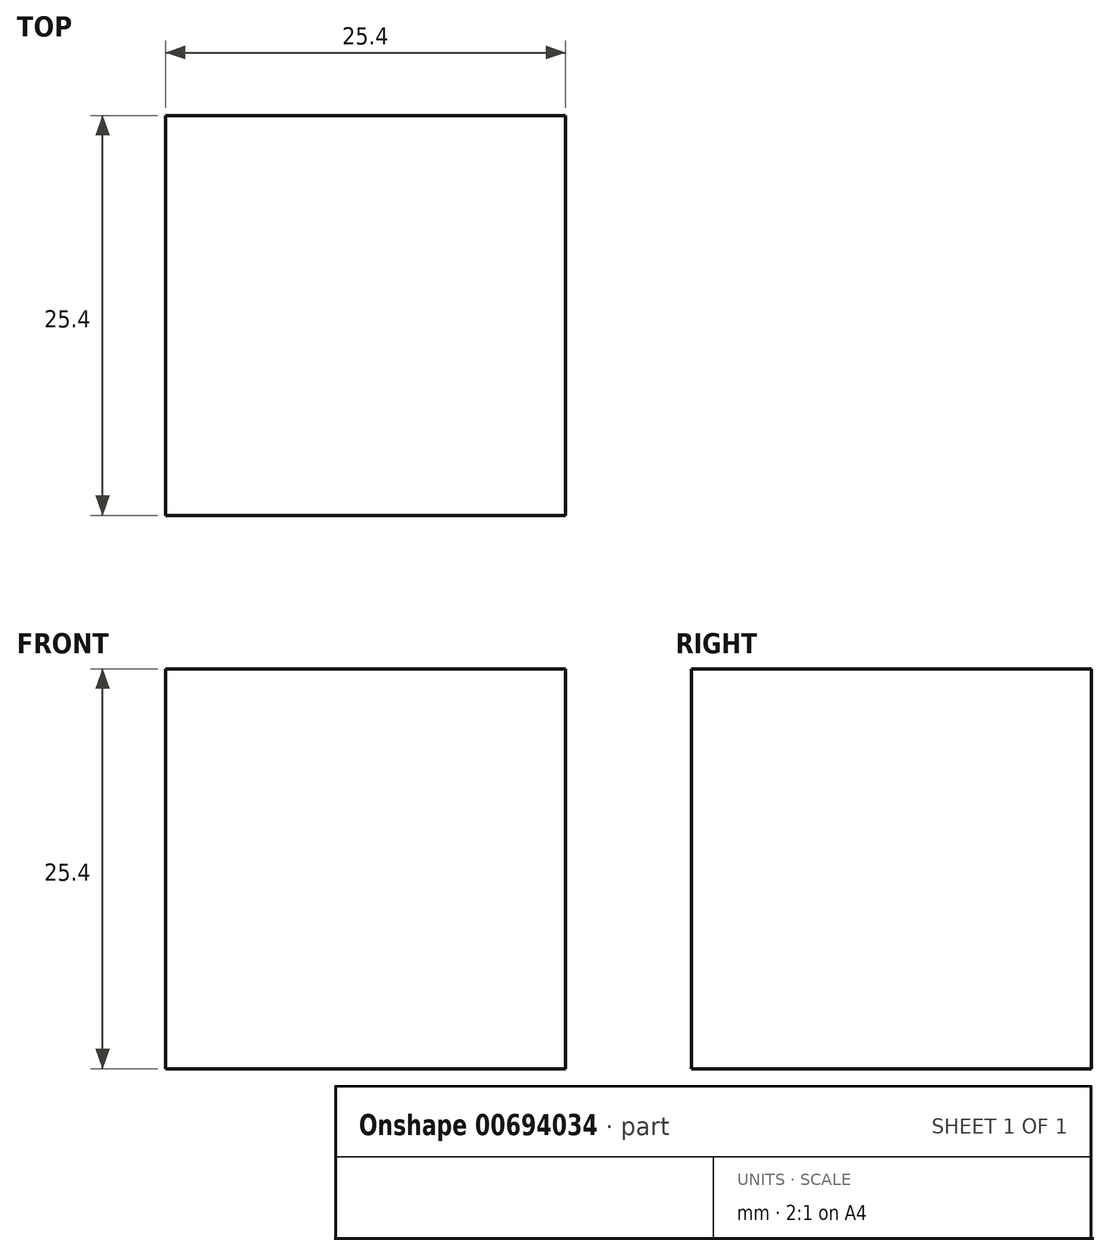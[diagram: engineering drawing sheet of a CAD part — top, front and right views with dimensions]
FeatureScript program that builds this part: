
annotation { "Feature Type Name" : "Feature", "Feature Type Description" : "" }
export const myFeature = defineFeature(function(context is Context, id is Id, definition is map)
    precondition{}
    {
        {
            var Q0;
            Q0=qCreatedBy(makeId("Top.planeOp"),FACE);
            var sketch = newSketch(context, id + "F0", { "sketchPlane" : qUnion([Q0])});
            skLineSegment(sketch, "E0.bottom", {"start": v(12.7, 12.7) * mm, "end": v(-12.7, 12.7) * mm});
            skLineSegment(sketch, "E0.top", {"start": v(12.7, -12.7) * mm, "end": v(-12.7, -12.7) * mm});
            skLineSegment(sketch, "E0.left", {"start": v(12.7, 12.7) * mm, "end": v(12.7, -12.7) * mm});
            skLineSegment(sketch, "E0.right", {"start": v(-12.7, 12.7) * mm, "end": v(-12.7, -12.7) * mm});
            skPoint(sketch, "E0.middle", {"position": v(0, 0) * mm});
            skSolve(sketch);
        }
        {
            var Q0;
            Q0 = qSketchRegion(id + "F0", true);
            extrude(context, id + "F1", {"entities" : qUnion([Q0]), "depth" : 25.4 * mm, "offsetDistance" : 25.4 * mm});
        }
    });
